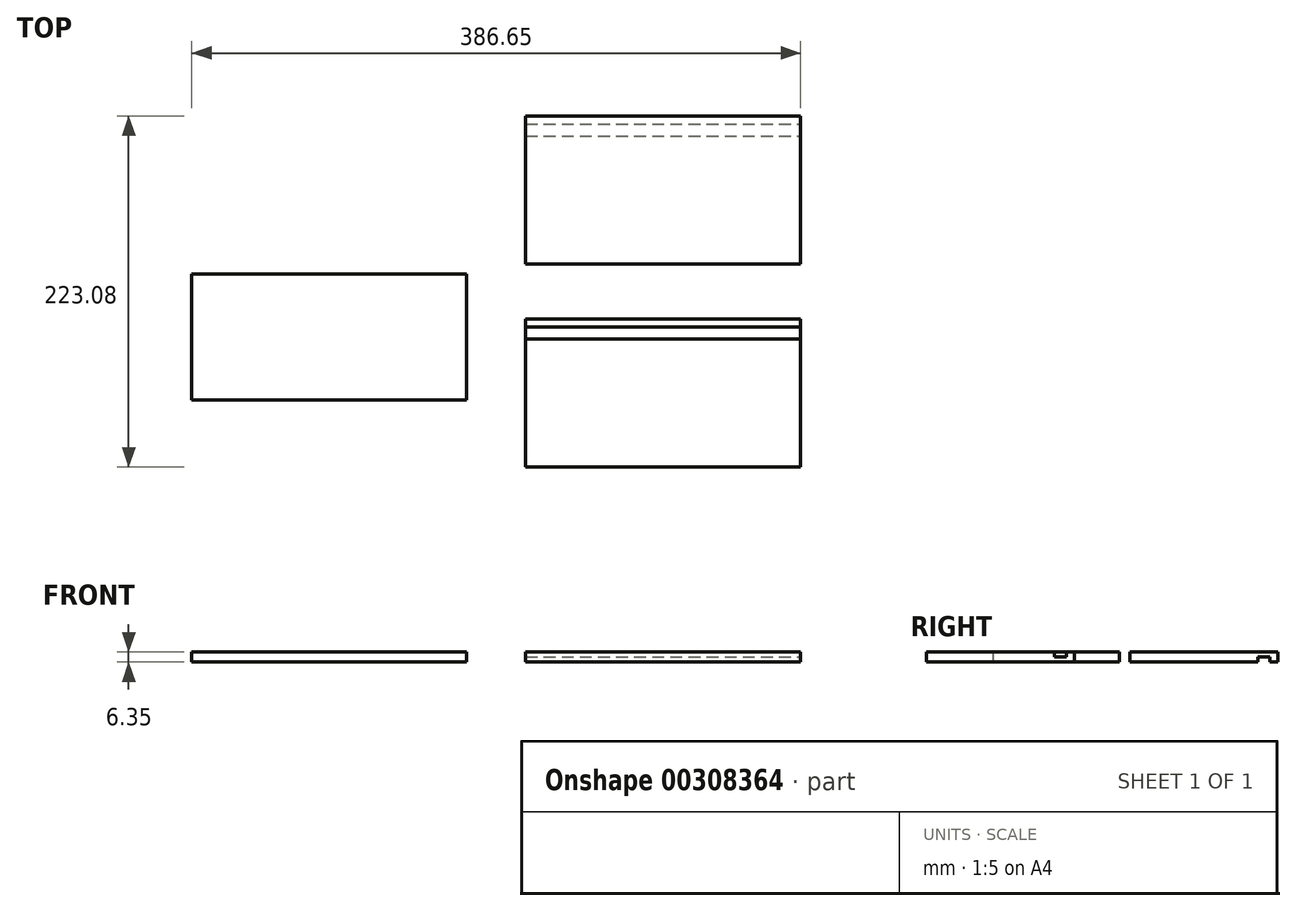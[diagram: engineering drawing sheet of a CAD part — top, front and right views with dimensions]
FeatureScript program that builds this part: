
annotation { "Feature Type Name" : "Feature", "Feature Type Description" : "" }
export const myFeature = defineFeature(function(context is Context, id is Id, definition is map)
    precondition{}
    {
        {
            var Q0;
            Q0=qCreatedBy(makeId("Top.planeOp"),FACE);
            var sketch = newSketch(context, id + "F0", { "sketchPlane" : qUnion([Q0])});
            skLineSegment(sketch, "E0.bottom", {"start": v(-89.97, 32.6) * mm, "end": v(84.66, 32.6) * mm});
            skLineSegment(sketch, "E0.top", {"start": v(-89.97, -61.38) * mm, "end": v(84.66, -61.38) * mm});
            skLineSegment(sketch, "E0.left", {"start": v(-89.97, 32.6) * mm, "end": v(-89.97, -61.38) * mm});
            skLineSegment(sketch, "E0.right", {"start": v(84.66, 32.6) * mm, "end": v(84.66, -61.38) * mm});
            skLineSegment(sketch, "E1", {"start": v(-107.6, 50.16) * mm, "end": v(120.28, 50.16) * mm});
            skLineSegment(sketch, "E2.MirrorCS", {"start": v(-89.97, 67.72) * mm, "end": v(-89.97, 161.7) * mm});
            skLineSegment(sketch, "E3.MirrorCS", {"start": v(-89.97, 161.7) * mm, "end": v(84.66, 161.7) * mm});
            skLineSegment(sketch, "E4.MirrorCS", {"start": v(-89.97, 67.72) * mm, "end": v(84.66, 67.72) * mm});
            skLineSegment(sketch, "E5.MirrorCS", {"start": v(84.66, 67.72) * mm, "end": v(84.66, 161.7) * mm});
            skSolve(sketch);
        }
        {
            var Q0;
            Q0 = qSketchRegion(id + "F0", true);
            extrude(context, id + "F1", {"entities" : qUnion([Q0]), "oppositeDirection" : true, "depth" : 6.35 * mm});
        }
        {
            var Q0;
            Q0=qCreatedBy(makeId("Top.planeOp"),FACE);
            var sketch = newSketch(context, id + "F2", { "sketchPlane" : qUnion([Q0])});
            skLineSegment(sketch, "E6.bottom", {"start": v(-302, 61.24) * mm, "end": v(-127.37, 61.24) * mm});
            skLineSegment(sketch, "E6.top", {"start": v(-302, -18.77) * mm, "end": v(-127.37, -18.77) * mm});
            skLineSegment(sketch, "E6.left", {"start": v(-302, 61.24) * mm, "end": v(-302, -18.77) * mm});
            skLineSegment(sketch, "E6.right", {"start": v(-127.37, 61.24) * mm, "end": v(-127.37, -18.77) * mm});
            skSolve(sketch);
        }
        {
            var Q0;
            Q0 = qSketchRegion(id + "F2", true);
            extrude(context, id + "F3", {"entities" : qUnion([Q0]), "oppositeDirection" : true, "depth" : 6.35 * mm});
        }
        {
            var Q0;
            Q0=makeQuery(id+"F1.opExtrude","CAP_FACE",FACE,{"disambiguationData":[OSD([sQuery(id+"F0.wireOp",EDGE,"E0.bottom"),sQuery(id+"F0.wireOp",EDGE,"E0.top"),sQuery(id+"F0.wireOp",EDGE,"E0.left"),sQuery(id+"F0.wireOp",EDGE,"E0.right")])],"isStart":true});
            var sketch = newSketch(context, id + "F4", { "sketchPlane" : qUnion([Q0])});
            skLineSegment(sketch, "E7.bottom", {"start": v(-89.97, 27.52) * mm, "end": v(84.66, 27.52) * mm});
            skLineSegment(sketch, "E7.top", {"start": v(-89.97, 19.9) * mm, "end": v(84.66, 19.9) * mm});
            skLineSegment(sketch, "E7.left", {"start": v(-89.97, 27.52) * mm, "end": v(-89.97, 19.9) * mm});
            skLineSegment(sketch, "E7.right", {"start": v(84.66, 27.52) * mm, "end": v(84.66, 19.9) * mm});
            skSolve(sketch);
        }
        {
            var Q0;
            Q0 = qSketchRegion(id + "F4", true);
            extrude(context, id + "F5", {"entities" : qUnion([Q0]), "operationType" : NewBodyOperationType.REMOVE, "oppositeDirection" : true, "depth" : 3.17 * mm});
        }
        {
            var Q0;
            Q0=makeQuery(id+"F1.opExtrude","CAP_FACE",FACE,{"disambiguationData":[OSD([sQuery(id+"F0.wireOp",EDGE,"E2.MirrorCS"),sQuery(id+"F0.wireOp",EDGE,"E3.MirrorCS"),sQuery(id+"F0.wireOp",EDGE,"E4.MirrorCS"),sQuery(id+"F0.wireOp",EDGE,"E5.MirrorCS")])],"isStart":false});
            var sketch = newSketch(context, id + "F6", { "sketchPlane" : qUnion([Q0])});
            skLineSegment(sketch, "E8.bottom", {"start": v(-89.97, -149) * mm, "end": v(84.66, -149) * mm});
            skLineSegment(sketch, "E8.top", {"start": v(-89.97, -156.62) * mm, "end": v(84.66, -156.62) * mm});
            skLineSegment(sketch, "E8.left", {"start": v(-89.97, -149) * mm, "end": v(-89.97, -156.62) * mm});
            skLineSegment(sketch, "E8.right", {"start": v(84.66, -149) * mm, "end": v(84.66, -156.62) * mm});
            skSolve(sketch);
        }
        {
            var Q0;
            Q0 = qSketchRegion(id + "F6", true);
            extrude(context, id + "F7", {"entities" : qUnion([Q0]), "operationType" : NewBodyOperationType.REMOVE, "oppositeDirection" : true, "depth" : 3.17 * mm});
        }
    });
